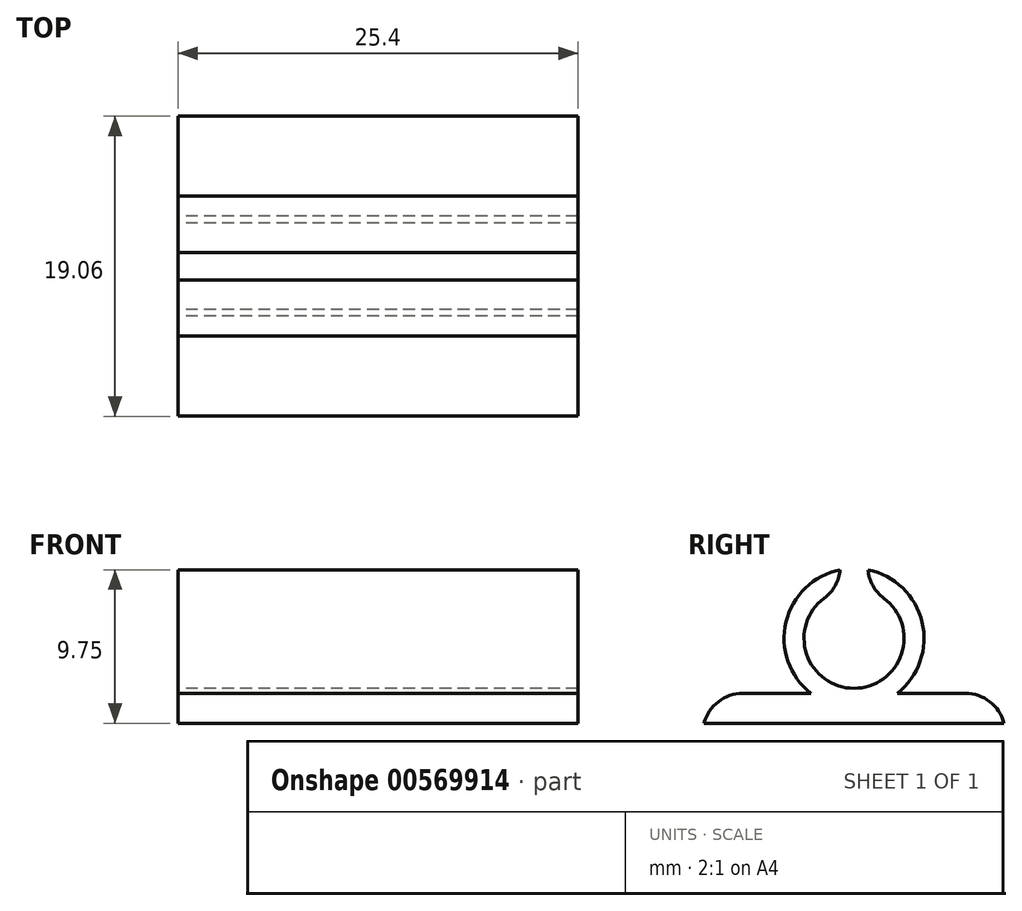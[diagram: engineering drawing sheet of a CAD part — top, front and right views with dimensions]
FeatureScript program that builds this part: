
annotation { "Feature Type Name" : "Feature", "Feature Type Description" : "" }
export const myFeature = defineFeature(function(context is Context, id is Id, definition is map)
    precondition{}
    {
        {
            var Q0;
            Q0=qCreatedBy(makeId("Top.planeOp"),FACE);
            var sketch = newSketch(context, id + "F0", { "sketchPlane" : qUnion([Q0])});
            skLineSegment(sketch, "E0.bottom", {"start": v(-12.7, 9.53) * mm, "end": v(12.7, 9.53) * mm});
            skLineSegment(sketch, "E0.top", {"start": v(-12.7, -9.53) * mm, "end": v(12.7, -9.53) * mm});
            skLineSegment(sketch, "E0.left", {"start": v(-12.7, 9.53) * mm, "end": v(-12.7, -9.53) * mm});
            skLineSegment(sketch, "E0.right", {"start": v(12.7, 9.53) * mm, "end": v(12.7, -9.53) * mm});
            skPoint(sketch, "E0.middle", {"position": v(0, 0) * mm});
            skSolve(sketch);
        }
        {
            var Q0;
            Q0=makeQuery(id+"F0.imprint","IMPRINT",FACE,{"disambiguationData":[TD([[makeQuery(id+"F0.imprint","IMPRINT",EDGE,{"derivedFrom":sQuery(id+"F0.wireOp",EDGE,"E0.bottom")}),-1.0]])]});
            extrude(context, id + "F1", {"entities" : qUnion([Q0]), "depth" : 1.9 * mm, "offsetDistance" : 25.4 * mm});
        }
        {
            var Q0;
            Q0=qCreatedBy(makeId("Right.planeOp"),FACE);
            var sketch = newSketch(context, id + "F2", { "sketchPlane" : qUnion([Q0])});
            skLineSegment(sketch, "E1.0.0", {"start": v(-9.53, 0) * mm, "end": v(9.53, 0) * mm});
            skLineSegment(sketch, "E1.0.1", {"start": v(9.53, 0) * mm, "end": v(9.53, 1.9) * mm});
            skLineSegment(sketch, "E1.0.2", {"start": v(9.53, 1.9) * mm, "end": v(-9.53, 1.9) * mm});
            skLineSegment(sketch, "E1.0.3", {"start": v(-9.53, 1.9) * mm, "end": v(-9.53, 0) * mm});
            skPoint(sketch, "E2.first.point", {"position": v(0, 1.9) * mm});
            skPoint(sketch, "E2.third.point.positionSnap0", {"position": v(0, 1.9) * mm});
            skCircle(sketch, "E3", {"center": v(0, 5.4) * mm, "radius": 4.45 * mm});
            skPoint(sketch, "E3.first.point", {"position": v(0, 0.95) * mm});
            skPoint(sketch, "E3.second.point", {"position": v(4, 7.33) * mm});
            skPoint(sketch, "E3.third.point", {"position": v(-1.21, 9.67) * mm});
            skLineSegment(sketch, "E4", {"start": v(0, 5.4) * mm, "end": v(0, 0) * mm, "construction": true});
            skLineSegment(sketch, "E5", {"start": v(-9.53, 0.95) * mm, "end": v(9.53, 0.95) * mm, "construction": true});
            skCircle(sketch, "E6", {"center": v(0, 5.4) * mm, "radius": 3.18 * mm});
            skLineSegment(sketch, "E7", {"start": v(-0.88, 8.45) * mm, "end": v(-0.88, 9.75) * mm});
            skLineSegment(sketch, "E8", {"start": v(0.88, 8.45) * mm, "end": v(0.88, 9.75) * mm});
            skSolve(sketch);
        }
        {
            var Q0;
            {var subQ5=sQuery(id+"F2.wireOp",EDGE,"E8");Q0=makeQuery(id+"F2.imprint","IMPRINT",FACE,{"disambiguationData":[TD([[makeQuery(id+"F2.imprint","IMPRINT",EDGE,{"derivedFrom":subQ5}),-1.0]])]});}
            var Q1;
            {var subQ5=sQuery(id+"F2.wireOp",EDGE,"E7");Q1=makeQuery(id+"F2.imprint","IMPRINT",FACE,{"disambiguationData":[TD([[makeQuery(id+"F2.imprint","IMPRINT",EDGE,{"derivedFrom":subQ5}),1.0]])]});}
            var Q2;
            Q2=sQuery(id+"F2.wireOp",EDGE,"E2");
            extrude(context, id + "F3", {"entities" : qUnion([Q0, Q1]), "operationType" : NewBodyOperationType.ADD, "surfaceEntities" : qUnion([Q2]), "endBound" : BoundingType.SYMMETRIC, "depth" : 25.4 * mm, "offsetDistance" : 25.4 * mm});
        }
        {
            var Q0;
            Q0=makeQuery(id+"F1.opExtrude","CAP_EDGE",EDGE,{"disambiguationData":[OSD([sQuery(id+"F0.wireOp",EDGE,"E0.top")])],"isStart":false});
            var Q1;
            Q1=makeQuery(id+"F1.opExtrude","CAP_EDGE",EDGE,{"disambiguationData":[OSD([sQuery(id+"F0.wireOp",EDGE,"E0.bottom")])],"isStart":false});
            var Q2;
            Q2=makeQuery(id+"F3.opExtrude","SWEPT_EDGE",EDGE,{"disambiguationData":[OSD([sQuery(id+"F2.wireOp",EDGE,"E6"),sQuery(id+"F2.wireOp",EDGE,"E8")])]});
            var Q3;
            Q3=makeQuery(id+"F3.opExtrude","SWEPT_EDGE",EDGE,{"disambiguationData":[OSD([sQuery(id+"F2.wireOp",EDGE,"E6"),sQuery(id+"F2.wireOp",EDGE,"E7")])]});
            fillet(context, id + "F4", {"entities" : qUnion([Q0, Q1, Q2, Q3]), "radius" : 2.54 * mm, "tangentPropagation" : true, "allowEdgeOverflow" : false});
        }
    });
